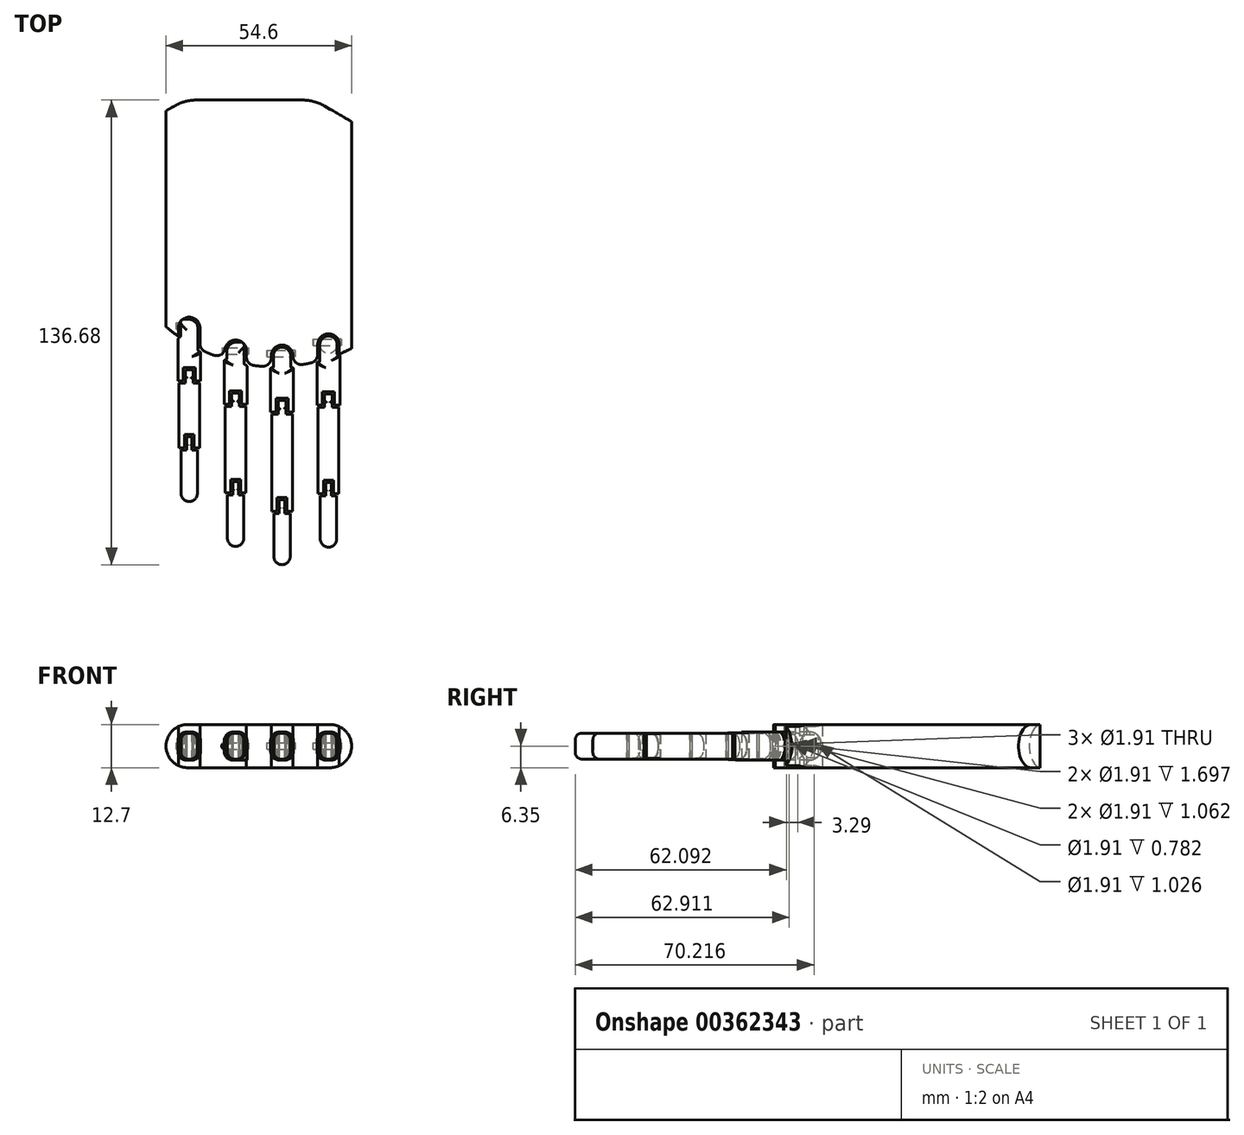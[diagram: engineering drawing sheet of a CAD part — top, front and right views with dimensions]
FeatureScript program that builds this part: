
annotation { "Feature Type Name" : "Feature", "Feature Type Description" : "" }
export const myFeature = defineFeature(function(context is Context, id is Id, definition is map)
    precondition{}
    {
        {
            var Q0;
            Q0=qCreatedBy(makeId("Top.planeOp"),FACE);
            var sketch = newSketch(context, id + "F0", { "sketchPlane" : qUnion([Q0])});
            skLineSegment(sketch, "E0", {"start": v(-15.65, 0) * mm, "end": v(15.65, 0) * mm});
            skLineSegment(sketch, "E1", {"start": v(-22, -1.7) * mm, "end": v(-24.55, -3.17) * mm});
            skLineSegment(sketch, "E2", {"start": v(22, -1.7) * mm, "end": v(30.05, -6.35) * mm});
            skPoint(sketch, "E3.visualSharp", {"position": v(-19.05, 0) * mm});
            skArc(sketch, "E3.filletArc", {"start": v(-15.65, 0) * mm, "mid": v(-18.93, -0.43) * mm, "end": v(-22, -1.7) * mm});
            skPoint(sketch, "E4.visualSharp", {"position": v(19.05, 0) * mm});
            skArc(sketch, "E4.filletArc", {"start": v(22, -1.7) * mm, "mid": v(18.93, -0.43) * mm, "end": v(15.65, 0) * mm});
            skLineSegment(sketch, "E5", {"start": v(-24.55, -3.17) * mm, "end": v(-24.55, -66.68) * mm});
            skLineSegment(sketch, "E6", {"start": v(30.05, -6.35) * mm, "end": v(30.05, -73.03) * mm});
            skArc(sketch, "E7", {"start": v(-24.55, -66.68) * mm, "mid": v(1.79, -78.13) * mm, "end": v(30.05, -73.03) * mm});
            skSolve(sketch);
        }
        {
            var Q0;
            Q0 = qSketchRegion(id + "F0", true);
            extrude(context, id + "F1", {"entities" : qUnion([Q0]), "depth" : 12.7 * mm});
        }
        {
            var Q0;
            Q0=makeQuery(id+"F1.opExtrude","CAP_FACE",FACE,{"disambiguationData":[OSD([sQuery(id+"F0.wireOp",EDGE,"E0"),sQuery(id+"F0.wireOp",EDGE,"E1"),sQuery(id+"F0.wireOp",EDGE,"E2"),sQuery(id+"F0.wireOp",EDGE,"E3.filletArc"),sQuery(id+"F0.wireOp",EDGE,"E4.filletArc"),sQuery(id+"F0.wireOp",EDGE,"E5"),sQuery(id+"F0.wireOp",EDGE,"E6"),sQuery(id+"F0.wireOp",EDGE,"E7")])],"isStart":false});
            var sketch = newSketch(context, id + "F2", { "sketchPlane" : qUnion([Q0])});
            skLineSegment(sketch, "E8.bottom", {"start": v(20.05, -68.76) * mm, "end": v(26.4, -68.76) * mm});
            skLineSegment(sketch, "E8.top", {"start": v(20.05, -81.46) * mm, "end": v(26.4, -81.46) * mm});
            skLineSegment(sketch, "E8.left", {"start": v(20.05, -68.76) * mm, "end": v(20.05, -81.46) * mm});
            skLineSegment(sketch, "E8.right", {"start": v(26.4, -68.76) * mm, "end": v(26.4, -81.46) * mm});
            skLineSegment(sketch, "E9.bottom", {"start": v(6.4, -72.05) * mm, "end": v(12.75, -72.05) * mm});
            skLineSegment(sketch, "E9.top", {"start": v(6.4, -84.75) * mm, "end": v(12.75, -84.75) * mm});
            skLineSegment(sketch, "E9.left", {"start": v(6.4, -72.05) * mm, "end": v(6.4, -84.75) * mm});
            skLineSegment(sketch, "E9.right", {"start": v(12.75, -72.05) * mm, "end": v(12.75, -84.75) * mm});
            skLineSegment(sketch, "E10.bottom", {"start": v(-7.25, -70.6) * mm, "end": v(-0.9, -70.6) * mm});
            skLineSegment(sketch, "E10.top", {"start": v(-7.25, -83.3) * mm, "end": v(-0.9, -83.3) * mm});
            skLineSegment(sketch, "E10.left", {"start": v(-7.25, -70.6) * mm, "end": v(-7.25, -83.3) * mm});
            skLineSegment(sketch, "E10.right", {"start": v(-0.9, -70.6) * mm, "end": v(-0.9, -83.3) * mm});
            skLineSegment(sketch, "E11.bottom", {"start": v(-20.9, -63.86) * mm, "end": v(-14.55, -63.86) * mm});
            skLineSegment(sketch, "E11.top", {"start": v(-20.9, -76.56) * mm, "end": v(-14.55, -76.56) * mm});
            skLineSegment(sketch, "E11.left", {"start": v(-20.9, -63.86) * mm, "end": v(-20.9, -76.56) * mm});
            skLineSegment(sketch, "E11.right", {"start": v(-14.55, -63.86) * mm, "end": v(-14.55, -76.56) * mm});
            skLineSegment(sketch, "E12", {"start": v(-24.55, -66.68) * mm, "end": v(30.05, -66.68) * mm, "construction": true});
            skLineSegment(sketch, "E13", {"start": v(-24.55, -70.2) * mm, "end": v(30.05, -70.2) * mm, "construction": true});
            skLineSegment(sketch, "E14", {"start": v(-10.78, -76.94) * mm, "end": v(0, -76.94) * mm, "construction": true});
            skLineSegment(sketch, "E15", {"start": v(14.95, -78.4) * mm, "end": v(7.26, -78.4) * mm, "construction": true});
            skLineSegment(sketch, "E16", {"start": v(22.41, -75.1) * mm, "end": v(20.87, -75.1) * mm, "construction": true});
            skLineSegment(sketch, "E17", {"start": v(-19.32, -68.57) * mm, "end": v(-19.32, -72.13) * mm, "construction": true});
            skLineSegment(sketch, "E18", {"start": v(-5.66, -75.3) * mm, "end": v(-5.66, -80.1) * mm, "construction": true});
            skLineSegment(sketch, "E19", {"start": v(7.99, -77.42) * mm, "end": v(7.99, -81.03) * mm, "construction": true});
            skLineSegment(sketch, "E20", {"start": v(21.64, -72.63) * mm, "end": v(21.64, -77.42) * mm, "construction": true});
            skPoint(sketch, "E20.startSnap0", {"position": v(21.64, -75.1) * mm});
            skSolve(sketch);
        }
        {
            var Q0;
            Q0 = qSketchRegion(id + "F2", true);
            extrude(context, id + "F3", {"entities" : qUnion([Q0]), "operationType" : NewBodyOperationType.REMOVE, "endBound" : BoundingType.UP_TO_NEXT, "oppositeDirection" : true, "depth" : 25.4 * mm});
        }
        {
            var Q0;
            Q0=qCreatedBy(makeId("Top.planeOp"),FACE);
            cPlane(context, id + "F4", {"entities" : qUnion([Q0]), "cplaneType" : CPlaneType.OFFSET, "offset" : 6.35 * mm, "width" : 152.4 * mm, "height" : 152.4 * mm});
        }
        {
            var Q0;
            Q0=qCreatedBy(id+"F4.planeOp",FACE);
            var sketch = newSketch(context, id + "F5", { "sketchPlane" : qUnion([Q0])});
            skLineSegment(sketch, "E21.bottom", {"start": v(-20.27, -64.5) * mm, "end": v(-15.19, -64.5) * mm});
            skLineSegment(sketch, "E21.left", {"start": v(-20.27, -64.5) * mm, "end": v(-20.27, -69.33) * mm});
            skLineSegment(sketch, "E21.right", {"start": v(-15.19, -64.5) * mm, "end": v(-15.19, -73.3) * mm});
            skLineSegment(sketch, "E22", {"start": v(-21.07, -70.6) * mm, "end": v(-21.07, -82.67) * mm});
            skLineSegment(sketch, "E23", {"start": v(-14.36, -82.67) * mm, "end": v(-14.36, -74.5) * mm});
            skArc(sketch, "E24", {"start": v(-14.84, -73.88) * mm, "mid": v(-14.78, -73.9) * mm, "end": v(-14.71, -73.94) * mm});
            skPoint(sketch, "E25.visualSharp", {"position": v(-15.19, -73.7) * mm});
            skArc(sketch, "E25.filletArc", {"start": v(-15.19, -73.3) * mm, "mid": v(-15.1, -73.64) * mm, "end": v(-14.84, -73.88) * mm});
            skPoint(sketch, "E26.visualSharp", {"position": v(-14.36, -74.11) * mm});
            skArc(sketch, "E26.filletArc", {"start": v(-14.36, -74.5) * mm, "mid": v(-14.46, -74.17) * mm, "end": v(-14.71, -73.94) * mm});
            skLineSegment(sketch, "E27", {"start": v(-21.07, -82.67) * mm, "end": v(-19.48, -82.67) * mm});
            skLineSegment(sketch, "E28", {"start": v(-19.48, -82.67) * mm, "end": v(-19.48, -78.69) * mm});
            skLineSegment(sketch, "E29", {"start": v(-19.48, -78.69) * mm, "end": v(-15.95, -78.69) * mm});
            skLineSegment(sketch, "E30", {"start": v(-15.95, -78.69) * mm, "end": v(-15.95, -82.67) * mm});
            skLineSegment(sketch, "E31", {"start": v(-15.95, -82.67) * mm, "end": v(-14.36, -82.67) * mm});
            skLineSegment(sketch, "E32.bottom", {"start": v(-6.62, -71.23) * mm, "end": v(-1.54, -71.23) * mm});
            skLineSegment(sketch, "E32.left", {"start": v(-6.62, -71.23) * mm, "end": v(-6.62, -75.87) * mm});
            skLineSegment(sketch, "E33", {"start": v(-1.54, -71.23) * mm, "end": v(-1.54, -77.58) * mm});
            skLineSegment(sketch, "E34", {"start": v(7.04, -78.4) * mm, "end": v(7.04, -72.68) * mm});
            skLineSegment(sketch, "E35", {"start": v(7.04, -72.68) * mm, "end": v(12.12, -72.68) * mm});
            skLineSegment(sketch, "E36", {"start": v(12.12, -72.68) * mm, "end": v(12.12, -78.4) * mm});
            skLineSegment(sketch, "E37", {"start": v(20.69, -76.73) * mm, "end": v(20.69, -69.4) * mm});
            skLineSegment(sketch, "E38", {"start": v(20.69, -69.4) * mm, "end": v(25.77, -69.4) * mm});
            skLineSegment(sketch, "E39", {"start": v(25.77, -69.4) * mm, "end": v(25.77, -74.6) * mm});
            skPoint(sketch, "E40.visualSharp", {"position": v(-21.07, -69.97) * mm});
            skPoint(sketch, "E41.visualSharp", {"position": v(-20.27, -69.97) * mm});
            skLineSegment(sketch, "E42", {"start": v(-7.43, -76.84) * mm, "end": v(-7.43, -89.54) * mm});
            skLineSegment(sketch, "E43", {"start": v(-7.43, -89.54) * mm, "end": v(-5.84, -89.54) * mm});
            skLineSegment(sketch, "E44", {"start": v(-5.84, -89.54) * mm, "end": v(-5.84, -85.55) * mm});
            skLineSegment(sketch, "E45", {"start": v(-5.84, -85.55) * mm, "end": v(-2.31, -85.55) * mm});
            skLineSegment(sketch, "E46", {"start": v(-2.31, -85.55) * mm, "end": v(-2.31, -89.54) * mm});
            skLineSegment(sketch, "E47", {"start": v(-2.31, -89.54) * mm, "end": v(-0.72, -89.54) * mm});
            skLineSegment(sketch, "E48", {"start": v(-0.72, -89.54) * mm, "end": v(-0.72, -78.5) * mm});
            skPoint(sketch, "E49.visualSharp", {"position": v(-6.62, -76.4) * mm});
            skPoint(sketch, "E50.visualSharp", {"position": v(-7.43, -76.4) * mm});
            skPoint(sketch, "E51.visualSharp", {"position": v(-1.54, -78.22) * mm});
            skArc(sketch, "E51.filletArc", {"start": v(-1.54, -77.58) * mm, "mid": v(-1.37, -77.79) * mm, "end": v(-1.13, -77.91) * mm});
            skPoint(sketch, "E52.visualSharp", {"position": v(-0.72, -78.22) * mm});
            skArc(sketch, "E52.filletArc", {"start": v(-0.72, -78.5) * mm, "mid": v(-0.84, -78.15) * mm, "end": v(-1.13, -77.91) * mm});
            skLineSegment(sketch, "E53.bottom", {"start": v(6.54, -78.72) * mm, "end": v(6.72, -78.72) * mm});
            skLineSegment(sketch, "E53.left", {"start": v(6.22, -79.03) * mm, "end": v(6.22, -91.73) * mm});
            skLineSegment(sketch, "E53.right", {"start": v(12.93, -79.03) * mm, "end": v(12.93, -91.73) * mm});
            skLineSegment(sketch, "E54.trimOffspring", {"start": v(12.43, -78.72) * mm, "end": v(12.61, -78.72) * mm});
            skPoint(sketch, "E55.visualSharp", {"position": v(7.04, -78.72) * mm});
            skArc(sketch, "E55.filletArc", {"start": v(6.72, -78.72) * mm, "mid": v(6.94, -78.62) * mm, "end": v(7.04, -78.4) * mm});
            skPoint(sketch, "E56.visualSharp", {"position": v(12.12, -78.72) * mm});
            skArc(sketch, "E56.filletArc", {"start": v(12.12, -78.4) * mm, "mid": v(12.2, -78.62) * mm, "end": v(12.43, -78.72) * mm});
            skLineSegment(sketch, "E57", {"start": v(6.22, -91.73) * mm, "end": v(7.81, -91.73) * mm});
            skLineSegment(sketch, "E58", {"start": v(7.81, -91.73) * mm, "end": v(7.81, -87.75) * mm});
            skLineSegment(sketch, "E59", {"start": v(7.81, -87.75) * mm, "end": v(11.34, -87.75) * mm});
            skLineSegment(sketch, "E60", {"start": v(11.34, -87.75) * mm, "end": v(11.34, -91.73) * mm});
            skLineSegment(sketch, "E61", {"start": v(11.34, -91.73) * mm, "end": v(12.93, -91.73) * mm});
            skPoint(sketch, "E62.visualSharp", {"position": v(6.22, -78.72) * mm});
            skArc(sketch, "E62.filletArc", {"start": v(6.54, -78.72) * mm, "mid": v(6.32, -78.8) * mm, "end": v(6.22, -79.03) * mm});
            skPoint(sketch, "E63.visualSharp", {"position": v(12.93, -78.72) * mm});
            skArc(sketch, "E63.filletArc", {"start": v(12.93, -79.03) * mm, "mid": v(12.84, -78.8) * mm, "end": v(12.61, -78.72) * mm});
            skArc(sketch, "E64", {"start": v(-7.03, -76.36) * mm, "mid": v(-6.73, -76.19) * mm, "end": v(-6.62, -75.87) * mm});
            skArc(sketch, "E65", {"start": v(-7.03, -76.36) * mm, "mid": v(-7.32, -76.53) * mm, "end": v(-7.43, -76.84) * mm});
            skArc(sketch, "E66", {"start": v(-20.67, -69.88) * mm, "mid": v(-20.96, -70.2) * mm, "end": v(-21.07, -70.6) * mm});
            skArc(sketch, "E67", {"start": v(-20.67, -69.88) * mm, "mid": v(-20.38, -69.67) * mm, "end": v(-20.27, -69.33) * mm});
            skLineSegment(sketch, "E68", {"start": v(20.37, -77.04) * mm, "end": v(20.2, -77.04) * mm});
            skLineSegment(sketch, "E69", {"start": v(19.88, -77.36) * mm, "end": v(19.88, -89.74) * mm});
            skLineSegment(sketch, "E70", {"start": v(19.88, -89.74) * mm, "end": v(21.46, -89.74) * mm});
            skLineSegment(sketch, "E71", {"start": v(21.46, -89.74) * mm, "end": v(21.46, -85.76) * mm});
            skLineSegment(sketch, "E72", {"start": v(21.46, -85.76) * mm, "end": v(25, -85.76) * mm});
            skLineSegment(sketch, "E73", {"start": v(25, -85.76) * mm, "end": v(25, -89.74) * mm});
            skLineSegment(sketch, "E74", {"start": v(25, -89.74) * mm, "end": v(26.58, -89.74) * mm});
            skLineSegment(sketch, "E75", {"start": v(26.58, -89.74) * mm, "end": v(26.58, -75.24) * mm});
            skLineSegment(sketch, "E76", {"start": v(26.26, -74.92) * mm, "end": v(26.09, -74.92) * mm});
            skPoint(sketch, "E77.visualSharp", {"position": v(19.88, -77.04) * mm});
            skArc(sketch, "E77.filletArc", {"start": v(20.2, -77.04) * mm, "mid": v(19.97, -77.14) * mm, "end": v(19.88, -77.36) * mm});
            skPoint(sketch, "E78.visualSharp", {"position": v(20.69, -77.04) * mm});
            skArc(sketch, "E78.filletArc", {"start": v(20.37, -77.04) * mm, "mid": v(20.6, -76.95) * mm, "end": v(20.69, -76.73) * mm});
            skPoint(sketch, "E79.visualSharp", {"position": v(25.77, -74.92) * mm});
            skArc(sketch, "E79.filletArc", {"start": v(25.77, -74.6) * mm, "mid": v(25.86, -74.83) * mm, "end": v(26.09, -74.92) * mm});
            skPoint(sketch, "E80.visualSharp", {"position": v(26.58, -74.92) * mm});
            skArc(sketch, "E80.filletArc", {"start": v(26.58, -75.24) * mm, "mid": v(26.49, -75.02) * mm, "end": v(26.26, -74.92) * mm});
            skSolve(sketch);
        }
        {
            var Q0;
            Q0 = qSketchRegion(id + "F5", true);
            extrude(context, id + "F6", {"entities" : qUnion([Q0]), "endBound" : BoundingType.SYMMETRIC, "depth" : 8.25 * mm});
        }
        {
            var Q0;
            Q0=makeQuery(id+"F6.opExtrude","CAP_EDGE",EDGE,{"disambiguationData":[OSD([sQuery(id+"F5.wireOp",EDGE,"E38")])],"isStart":false});
            var Q1;
            Q1=makeQuery(id+"F6.opExtrude","CAP_EDGE",EDGE,{"disambiguationData":[OSD([sQuery(id+"F5.wireOp",EDGE,"E38")])],"isStart":true});
            var Q2;
            Q2=makeQuery(id+"F6.opExtrude","CAP_EDGE",EDGE,{"disambiguationData":[OSD([sQuery(id+"F5.wireOp",EDGE,"E35")])],"isStart":false});
            var Q3;
            Q3=makeQuery(id+"F6.opExtrude","CAP_EDGE",EDGE,{"disambiguationData":[OSD([sQuery(id+"F5.wireOp",EDGE,"E35")])],"isStart":true});
            var Q4;
            Q4=makeQuery(id+"F6.opExtrude","CAP_EDGE",EDGE,{"disambiguationData":[OSD([sQuery(id+"F5.wireOp",EDGE,"E32.bottom")])],"isStart":true});
            var Q5;
            Q5=makeQuery(id+"F6.opExtrude","CAP_EDGE",EDGE,{"disambiguationData":[OSD([sQuery(id+"F5.wireOp",EDGE,"E21.bottom")])],"isStart":true});
            var Q6;
            Q6=makeQuery(id+"F6.opExtrude","CAP_EDGE",EDGE,{"disambiguationData":[OSD([sQuery(id+"F5.wireOp",EDGE,"E21.bottom")])],"isStart":false});
            var Q7;
            Q7=makeQuery(id+"F6.opExtrude","CAP_EDGE",EDGE,{"disambiguationData":[OSD([sQuery(id+"F5.wireOp",EDGE,"E32.bottom")])],"isStart":false});
            fillet(context, id + "F7", {"entities" : qUnion([Q0, Q1, Q2, Q3, Q4, Q5, Q6, Q7]), "radius" : 3.17 * mm, "tangentPropagation" : true, "allowEdgeOverflow" : false});
        }
        {
            var Q0;
            Q0=makeQuery(id+"F1.opExtrude","CAP_EDGE",EDGE,{"disambiguationData":[OSD([sQuery(id+"F0.wireOp",EDGE,"E5")])],"isStart":false});
            var Q1;
            Q1=makeQuery(id+"F1.opExtrude","CAP_EDGE",EDGE,{"disambiguationData":[OSD([sQuery(id+"F0.wireOp",EDGE,"E5")])],"isStart":true});
            var Q2;
            Q2=makeQuery(id+"F1.opExtrude","CAP_EDGE",EDGE,{"disambiguationData":[OSD([sQuery(id+"F0.wireOp",EDGE,"E6")])],"isStart":false});
            var Q3;
            Q3=makeQuery(id+"F1.opExtrude","CAP_EDGE",EDGE,{"disambiguationData":[OSD([sQuery(id+"F0.wireOp",EDGE,"E6")])],"isStart":true});
            fillet(context, id + "F8", {"entities" : qUnion([Q0, Q1, Q2, Q3]), "radius" : 6.35 * mm, "tangentPropagation" : true, "allowEdgeOverflow" : false});
        }
        {
            var Q0;
            Q0=makeQuery(id+"F3.boolean.opBoolean","COPY",EDGE,{"derivedFrom":makeQuery(id+"F3.opExtrude","SWEPT_EDGE",EDGE,{"disambiguationData":[OSD([sQuery(id+"F2.wireOp",EDGE,"E11.bottom"),sQuery(id+"F2.wireOp",EDGE,"E11.left")])]})});
            var Q1;
            Q1=makeQuery(id+"F3.boolean.opBoolean","COPY",EDGE,{"derivedFrom":makeQuery(id+"F3.opExtrude","SWEPT_EDGE",EDGE,{"disambiguationData":[OSD([sQuery(id+"F2.wireOp",EDGE,"E11.bottom"),sQuery(id+"F2.wireOp",EDGE,"E11.right")])]})});
            var Q2;
            Q2=makeQuery(id+"F3.boolean.opBoolean","COPY",EDGE,{"derivedFrom":makeQuery(id+"F3.opExtrude","SWEPT_EDGE",EDGE,{"disambiguationData":[OSD([sQuery(id+"F2.wireOp",EDGE,"E10.bottom"),sQuery(id+"F2.wireOp",EDGE,"E10.left")])]})});
            var Q3;
            Q3=makeQuery(id+"F3.boolean.opBoolean","COPY",EDGE,{"derivedFrom":makeQuery(id+"F3.opExtrude","SWEPT_EDGE",EDGE,{"disambiguationData":[OSD([sQuery(id+"F2.wireOp",EDGE,"E10.bottom"),sQuery(id+"F2.wireOp",EDGE,"E10.right")])]})});
            var Q4;
            Q4=makeQuery(id+"F3.boolean.opBoolean","COPY",EDGE,{"derivedFrom":makeQuery(id+"F3.opExtrude","SWEPT_EDGE",EDGE,{"disambiguationData":[OSD([sQuery(id+"F2.wireOp",EDGE,"E9.bottom"),sQuery(id+"F2.wireOp",EDGE,"E9.right")])]})});
            var Q5;
            Q5=makeQuery(id+"F3.boolean.opBoolean","COPY",EDGE,{"derivedFrom":makeQuery(id+"F3.opExtrude","SWEPT_EDGE",EDGE,{"disambiguationData":[OSD([sQuery(id+"F2.wireOp",EDGE,"E8.bottom"),sQuery(id+"F2.wireOp",EDGE,"E8.right")])]})});
            var Q6;
            Q6=makeQuery(id+"F3.boolean.opBoolean","COPY",EDGE,{"derivedFrom":makeQuery(id+"F3.opExtrude","SWEPT_EDGE",EDGE,{"disambiguationData":[OSD([sQuery(id+"F2.wireOp",EDGE,"E9.bottom"),sQuery(id+"F2.wireOp",EDGE,"E9.left")])]})});
            var Q7;
            Q7=makeQuery(id+"F3.boolean.opBoolean","COPY",EDGE,{"derivedFrom":makeQuery(id+"F3.opExtrude","SWEPT_EDGE",EDGE,{"disambiguationData":[OSD([sQuery(id+"F2.wireOp",EDGE,"E8.bottom"),sQuery(id+"F2.wireOp",EDGE,"E8.left")])]})});
            fillet(context, id + "F9", {"entities" : qUnion([Q0, Q1, Q2, Q3, Q4, Q5, Q6, Q7]), "radius" : 3.17 * mm, "tangentPropagation" : true, "allowEdgeOverflow" : false});
        }
        {
            var Q0;
            {var subQ0=sQuery(id+"F0.wireOp",EDGE,"E7");var subQ1=sQuery(id+"F2.wireOp",EDGE,"E10.left");Q0=makeQuery(id+"F3.boolean.opBoolean","COPY",EDGE,{"derivedFrom":makeQuery(id+"F3.opExtrude","CAP_EDGE",EDGE,{"disambiguationData":[OSD([subQ1]),topologyDisambiguationEdgeConnected([makeQuery(id+"F1.opExtrude","SWEPT_FACE",FACE,{"disambiguationData":[OSD([subQ0])]})])],"isStart":false})});}
            var Q1;
            Q1=makeQuery(id+"F3.boolean.opBoolean","COPY",EDGE,{"derivedFrom":makeQuery(id+"F3.opExtrude","CAP_EDGE",EDGE,{"disambiguationData":[OSD([sQuery(id+"F2.wireOp",EDGE,"E11.right")]),topologyDisambiguationEdgeConnected([makeQuery(id+"F1.opExtrude","SWEPT_FACE",FACE,{"disambiguationData":[OSD([sQuery(id+"F0.wireOp",EDGE,"E7")])]})])],"isStart":false})});
            var Q2;
            {var subQ0=sQuery(id+"F0.wireOp",EDGE,"E7");var subQ1=sQuery(id+"F2.wireOp",EDGE,"E10.right");Q2=makeQuery(id+"F3.boolean.opBoolean","COPY",EDGE,{"derivedFrom":makeQuery(id+"F3.opExtrude","CAP_EDGE",EDGE,{"disambiguationData":[OSD([subQ1]),topologyDisambiguationEdgeConnected([makeQuery(id+"F1.opExtrude","SWEPT_FACE",FACE,{"disambiguationData":[OSD([subQ0])]})])],"isStart":false})});}
            var Q3;
            {var subQ0=sQuery(id+"F0.wireOp",EDGE,"E7");var subQ1=sQuery(id+"F2.wireOp",EDGE,"E9.left");Q3=makeQuery(id+"F3.boolean.opBoolean","COPY",EDGE,{"derivedFrom":makeQuery(id+"F3.opExtrude","CAP_EDGE",EDGE,{"disambiguationData":[OSD([subQ1]),topologyDisambiguationEdgeConnected([makeQuery(id+"F1.opExtrude","SWEPT_FACE",FACE,{"disambiguationData":[OSD([subQ0])]})])],"isStart":false})});}
            var Q4;
            {var subQ0=sQuery(id+"F0.wireOp",EDGE,"E7");var subQ1=sQuery(id+"F2.wireOp",EDGE,"E9.right");Q4=makeQuery(id+"F3.boolean.opBoolean","COPY",EDGE,{"derivedFrom":makeQuery(id+"F3.opExtrude","CAP_EDGE",EDGE,{"disambiguationData":[OSD([subQ1]),topologyDisambiguationEdgeConnected([makeQuery(id+"F1.opExtrude","SWEPT_FACE",FACE,{"disambiguationData":[OSD([subQ0])]})])],"isStart":false})});}
            var Q5;
            {var subQ0=sQuery(id+"F0.wireOp",EDGE,"E7");var subQ1=sQuery(id+"F2.wireOp",EDGE,"E8.left");Q5=makeQuery(id+"F3.boolean.opBoolean","COPY",EDGE,{"derivedFrom":makeQuery(id+"F3.opExtrude","CAP_EDGE",EDGE,{"disambiguationData":[OSD([subQ1]),topologyDisambiguationEdgeConnected([makeQuery(id+"F1.opExtrude","SWEPT_FACE",FACE,{"disambiguationData":[OSD([subQ0])]})])],"isStart":false})});}
            fillet(context, id + "F10", {"entities" : qUnion([Q0, Q1, Q2, Q3, Q4, Q5]), "radius" : 2.54 * mm, "tangentPropagation" : true, "allowEdgeOverflow" : false});
        }
        {
            var Q0;
            Q0=makeQuery(id+"F6.opExtrude","CAP_EDGE",EDGE,{"disambiguationData":[OSD([sQuery(id+"F5.wireOp",EDGE,"E42")])],"isStart":false});
            var Q1;
            Q1=makeQuery(id+"F6.opExtrude","CAP_EDGE",EDGE,{"disambiguationData":[OSD([sQuery(id+"F5.wireOp",EDGE,"E48")])],"isStart":false});
            var Q2;
            Q2=makeQuery(id+"F6.opExtrude","CAP_EDGE",EDGE,{"disambiguationData":[OSD([sQuery(id+"F5.wireOp",EDGE,"E23")])],"isStart":false});
            var Q3;
            Q3=makeQuery(id+"F6.opExtrude","CAP_EDGE",EDGE,{"disambiguationData":[OSD([sQuery(id+"F5.wireOp",EDGE,"E22")])],"isStart":false});
            var Q4;
            Q4=makeQuery(id+"F6.opExtrude","CAP_EDGE",EDGE,{"disambiguationData":[OSD([sQuery(id+"F5.wireOp",EDGE,"E53.left")])],"isStart":false});
            var Q5;
            Q5=makeQuery(id+"F6.opExtrude","CAP_EDGE",EDGE,{"disambiguationData":[OSD([sQuery(id+"F5.wireOp",EDGE,"E53.right")])],"isStart":false});
            var Q6;
            Q6=makeQuery(id+"F6.opExtrude","CAP_EDGE",EDGE,{"disambiguationData":[OSD([sQuery(id+"F5.wireOp",EDGE,"E69")])],"isStart":false});
            var Q7;
            Q7=makeQuery(id+"F6.opExtrude","CAP_EDGE",EDGE,{"disambiguationData":[OSD([sQuery(id+"F5.wireOp",EDGE,"E75")])],"isStart":false});
            fillet(context, id + "F11", {"entities" : qUnion([Q0, Q1, Q2, Q3, Q4, Q5, Q6, Q7]), "radius" : 2.54 * mm, "tangentPropagation" : true, "allowEdgeOverflow" : false});
        }
        {
            var Q0;
            Q0=makeQuery(id+"F6.opExtrude","CAP_EDGE",EDGE,{"disambiguationData":[OSD([sQuery(id+"F5.wireOp",EDGE,"E22")])],"isStart":true});
            fillet(context, id + "F12", {"entities" : qUnion([Q0]), "radius" : 2.54 * mm, "tangentPropagation" : true, "allowEdgeOverflow" : false});
        }
        {
            var Q0;
            Q0=qCreatedBy(id+"F4.planeOp",FACE);
            var sketch = newSketch(context, id + "F13", { "sketchPlane" : qUnion([Q0])});
            skLineSegment(sketch, "E81.bottom", {"start": v(-18.85, -79.32) * mm, "end": v(-16.59, -79.32) * mm});
            skLineSegment(sketch, "E81.left", {"start": v(-18.85, -79.32) * mm, "end": v(-18.85, -83.3) * mm});
            skLineSegment(sketch, "E81.right", {"start": v(-16.59, -79.32) * mm, "end": v(-16.59, -83.3) * mm});
            skLineSegment(sketch, "E82", {"start": v(-18.85, -83.3) * mm, "end": v(-20.75, -83.3) * mm});
            skLineSegment(sketch, "E83", {"start": v(-20.75, -83.3) * mm, "end": v(-20.75, -102.35) * mm});
            skLineSegment(sketch, "E84", {"start": v(-20.75, -102.35) * mm, "end": v(-19.16, -102.35) * mm});
            skLineSegment(sketch, "E85", {"start": v(-14.68, -102.35) * mm, "end": v(-14.68, -83.3) * mm});
            skLineSegment(sketch, "E86", {"start": v(-14.68, -83.3) * mm, "end": v(-16.59, -83.3) * mm});
            skLineSegment(sketch, "E87.top", {"start": v(-19.16, -98.36) * mm, "end": v(-16.27, -98.36) * mm});
            skLineSegment(sketch, "E87.left", {"start": v(-19.16, -102.35) * mm, "end": v(-19.16, -98.36) * mm});
            skLineSegment(sketch, "E87.right", {"start": v(-16.27, -102.35) * mm, "end": v(-16.27, -98.36) * mm});
            skLineSegment(sketch, "E88.trimOffspring", {"start": v(-16.27, -102.35) * mm, "end": v(-14.68, -102.35) * mm});
            skLineSegment(sketch, "E89.bottom", {"start": v(-5.2, -86.18) * mm, "end": v(-2.95, -86.18) * mm});
            skLineSegment(sketch, "E89.left", {"start": v(-5.2, -86.18) * mm, "end": v(-5.2, -90.17) * mm});
            skLineSegment(sketch, "E89.right", {"start": v(-2.95, -86.18) * mm, "end": v(-2.95, -90.17) * mm});
            skLineSegment(sketch, "E90.bottom", {"start": v(-7.11, -90.17) * mm, "end": v(-5.2, -90.17) * mm});
            skLineSegment(sketch, "E90.top", {"start": v(-7.11, -115.57) * mm, "end": v(-5.52, -115.57) * mm});
            skLineSegment(sketch, "E90.left", {"start": v(-7.11, -90.17) * mm, "end": v(-7.11, -115.57) * mm});
            skLineSegment(sketch, "E90.right", {"start": v(-1.04, -90.17) * mm, "end": v(-1.04, -115.57) * mm});
            skLineSegment(sketch, "E91.bottom", {"start": v(-5.52, -111.58) * mm, "end": v(-2.63, -111.58) * mm});
            skLineSegment(sketch, "E91.left", {"start": v(-5.52, -111.58) * mm, "end": v(-5.52, -115.57) * mm});
            skLineSegment(sketch, "E91.right", {"start": v(-2.63, -111.58) * mm, "end": v(-2.63, -115.57) * mm});
            skLineSegment(sketch, "E92.bottom", {"start": v(8.45, -88.38) * mm, "end": v(10.7, -88.38) * mm});
            skLineSegment(sketch, "E92.left", {"start": v(8.45, -88.38) * mm, "end": v(8.45, -92.37) * mm});
            skLineSegment(sketch, "E92.right", {"start": v(10.7, -88.38) * mm, "end": v(10.7, -92.37) * mm});
            skLineSegment(sketch, "E93.bottom", {"start": v(6.54, -92.37) * mm, "end": v(8.45, -92.37) * mm});
            skLineSegment(sketch, "E93.top", {"start": v(6.54, -120.94) * mm, "end": v(8.13, -120.94) * mm});
            skLineSegment(sketch, "E93.left", {"start": v(6.54, -92.37) * mm, "end": v(6.54, -120.94) * mm});
            skLineSegment(sketch, "E93.right", {"start": v(12.61, -92.37) * mm, "end": v(12.61, -120.94) * mm});
            skLineSegment(sketch, "E94.bottom", {"start": v(8.13, -116.96) * mm, "end": v(11.02, -116.96) * mm});
            skLineSegment(sketch, "E94.left", {"start": v(8.13, -116.96) * mm, "end": v(8.13, -120.94) * mm});
            skLineSegment(sketch, "E94.right", {"start": v(11.02, -116.96) * mm, "end": v(11.02, -120.94) * mm});
            skLineSegment(sketch, "E95.bottom", {"start": v(22.1, -86.4) * mm, "end": v(24.36, -86.4) * mm});
            skLineSegment(sketch, "E95.left", {"start": v(22.1, -86.4) * mm, "end": v(22.1, -90.38) * mm});
            skLineSegment(sketch, "E95.right", {"start": v(24.36, -86.4) * mm, "end": v(24.36, -90.38) * mm});
            skLineSegment(sketch, "E96.bottom", {"start": v(20.2, -90.38) * mm, "end": v(22.1, -90.38) * mm});
            skLineSegment(sketch, "E96.top", {"start": v(20.2, -115.78) * mm, "end": v(21.78, -115.78) * mm});
            skLineSegment(sketch, "E96.left", {"start": v(20.2, -90.38) * mm, "end": v(20.2, -115.78) * mm});
            skLineSegment(sketch, "E96.right", {"start": v(26.26, -90.38) * mm, "end": v(26.26, -115.78) * mm});
            skLineSegment(sketch, "E97.bottom", {"start": v(21.78, -111.8) * mm, "end": v(24.68, -111.8) * mm});
            skLineSegment(sketch, "E97.left", {"start": v(21.78, -111.8) * mm, "end": v(21.78, -115.78) * mm});
            skLineSegment(sketch, "E97.right", {"start": v(24.68, -111.8) * mm, "end": v(24.68, -115.78) * mm});
            skLineSegment(sketch, "E98.trimOffspring", {"start": v(-2.95, -90.17) * mm, "end": v(-1.04, -90.17) * mm});
            skLineSegment(sketch, "E99.trimOffspring", {"start": v(-2.63, -115.57) * mm, "end": v(-1.04, -115.57) * mm});
            skLineSegment(sketch, "E100.trimOffspring", {"start": v(10.7, -92.37) * mm, "end": v(12.61, -92.37) * mm});
            skLineSegment(sketch, "E101.trimOffspring", {"start": v(11.02, -120.94) * mm, "end": v(12.61, -120.94) * mm});
            skLineSegment(sketch, "E102.trimOffspring", {"start": v(24.36, -90.38) * mm, "end": v(26.26, -90.38) * mm});
            skLineSegment(sketch, "E103.trimOffspring", {"start": v(24.68, -115.78) * mm, "end": v(26.26, -115.78) * mm});
            skSolve(sketch);
        }
        {
            var Q0;
            Q0 = qSketchRegion(id + "F13", true);
            extrude(context, id + "F14", {"entities" : qUnion([Q0]), "endBound" : BoundingType.SYMMETRIC, "depth" : 7.62 * mm});
        }
        {
            var Q0;
            Q0=makeQuery(id+"F14.opExtrude","CAP_EDGE",EDGE,{"disambiguationData":[OSD([sQuery(id+"F13.wireOp",EDGE,"E83")])],"isStart":false});
            var Q1;
            Q1=makeQuery(id+"F14.opExtrude","CAP_EDGE",EDGE,{"disambiguationData":[OSD([sQuery(id+"F13.wireOp",EDGE,"E85")])],"isStart":false});
            var Q2;
            Q2=makeQuery(id+"F14.opExtrude","CAP_EDGE",EDGE,{"disambiguationData":[OSD([sQuery(id+"F13.wireOp",EDGE,"E83")])],"isStart":true});
            var Q3;
            Q3=makeQuery(id+"F14.opExtrude","CAP_EDGE",EDGE,{"disambiguationData":[OSD([sQuery(id+"F13.wireOp",EDGE,"E85")])],"isStart":true});
            var Q4;
            Q4=makeQuery(id+"F14.opExtrude","CAP_EDGE",EDGE,{"disambiguationData":[OSD([sQuery(id+"F13.wireOp",EDGE,"E90.left")])],"isStart":true});
            var Q5;
            Q5=makeQuery(id+"F14.opExtrude","CAP_EDGE",EDGE,{"disambiguationData":[OSD([sQuery(id+"F13.wireOp",EDGE,"E90.right")])],"isStart":true});
            var Q6;
            Q6=makeQuery(id+"F14.opExtrude","CAP_EDGE",EDGE,{"disambiguationData":[OSD([sQuery(id+"F13.wireOp",EDGE,"E93.left")])],"isStart":true});
            var Q7;
            Q7=makeQuery(id+"F14.opExtrude","CAP_EDGE",EDGE,{"disambiguationData":[OSD([sQuery(id+"F13.wireOp",EDGE,"E93.right")])],"isStart":true});
            var Q8;
            Q8=makeQuery(id+"F14.opExtrude","CAP_EDGE",EDGE,{"disambiguationData":[OSD([sQuery(id+"F13.wireOp",EDGE,"E96.left")])],"isStart":true});
            var Q9;
            Q9=makeQuery(id+"F14.opExtrude","CAP_EDGE",EDGE,{"disambiguationData":[OSD([sQuery(id+"F13.wireOp",EDGE,"E96.right")])],"isStart":true});
            var Q10;
            Q10=makeQuery(id+"F14.opExtrude","CAP_EDGE",EDGE,{"disambiguationData":[OSD([sQuery(id+"F13.wireOp",EDGE,"E96.left")])],"isStart":false});
            var Q11;
            Q11=makeQuery(id+"F14.opExtrude","CAP_EDGE",EDGE,{"disambiguationData":[OSD([sQuery(id+"F13.wireOp",EDGE,"E96.right")])],"isStart":false});
            var Q12;
            Q12=makeQuery(id+"F14.opExtrude","CAP_EDGE",EDGE,{"disambiguationData":[OSD([sQuery(id+"F13.wireOp",EDGE,"E93.right")])],"isStart":false});
            var Q13;
            Q13=makeQuery(id+"F14.opExtrude","CAP_EDGE",EDGE,{"disambiguationData":[OSD([sQuery(id+"F13.wireOp",EDGE,"E93.left")])],"isStart":false});
            var Q14;
            Q14=makeQuery(id+"F14.opExtrude","CAP_EDGE",EDGE,{"disambiguationData":[OSD([sQuery(id+"F13.wireOp",EDGE,"E90.right")])],"isStart":false});
            var Q15;
            Q15=makeQuery(id+"F14.opExtrude","CAP_EDGE",EDGE,{"disambiguationData":[OSD([sQuery(id+"F13.wireOp",EDGE,"E90.left")])],"isStart":false});
            fillet(context, id + "F15", {"entities" : qUnion([Q0, Q1, Q2, Q3, Q4, Q5, Q6, Q7, Q8, Q9, Q10, Q11, Q12, Q13, Q14, Q15]), "radius" : 2.54 * mm, "tangentPropagation" : true, "allowEdgeOverflow" : false});
        }
        {
            var Q0;
            Q0=makeQuery(id+"F14.opExtrude","CAP_EDGE",EDGE,{"disambiguationData":[OSD([sQuery(id+"F13.wireOp",EDGE,"E81.bottom")])],"isStart":false});
            var Q1;
            Q1=makeQuery(id+"F14.opExtrude","CAP_EDGE",EDGE,{"disambiguationData":[OSD([sQuery(id+"F13.wireOp",EDGE,"E89.bottom")])],"isStart":false});
            var Q2;
            Q2=makeQuery(id+"F14.opExtrude","CAP_EDGE",EDGE,{"disambiguationData":[OSD([sQuery(id+"F13.wireOp",EDGE,"E92.bottom")])],"isStart":false});
            var Q3;
            Q3=makeQuery(id+"F14.opExtrude","CAP_EDGE",EDGE,{"disambiguationData":[OSD([sQuery(id+"F13.wireOp",EDGE,"E95.bottom")])],"isStart":false});
            var Q4;
            Q4=makeQuery(id+"F14.opExtrude","CAP_EDGE",EDGE,{"disambiguationData":[OSD([sQuery(id+"F13.wireOp",EDGE,"E95.bottom")])],"isStart":true});
            var Q5;
            Q5=makeQuery(id+"F14.opExtrude","CAP_EDGE",EDGE,{"disambiguationData":[OSD([sQuery(id+"F13.wireOp",EDGE,"E92.bottom")])],"isStart":true});
            var Q6;
            Q6=makeQuery(id+"F14.opExtrude","CAP_EDGE",EDGE,{"disambiguationData":[OSD([sQuery(id+"F13.wireOp",EDGE,"E89.bottom")])],"isStart":true});
            var Q7;
            Q7=makeQuery(id+"F14.opExtrude","CAP_EDGE",EDGE,{"disambiguationData":[OSD([sQuery(id+"F13.wireOp",EDGE,"E81.bottom")])],"isStart":true});
            fillet(context, id + "F16", {"entities" : qUnion([Q0, Q1, Q2, Q3, Q4, Q5, Q6, Q7]), "radius" : 2.54 * mm, "tangentPropagation" : true, "allowEdgeOverflow" : false});
        }
        {
            var Q0;
            Q0=qCreatedBy(id+"F4.planeOp",FACE);
            var sketch = newSketch(context, id + "F17", { "sketchPlane" : qUnion([Q0])});
            skLineSegment(sketch, "E104.bottom", {"start": v(-18.53, -99) * mm, "end": v(-16.9, -99) * mm});
            skLineSegment(sketch, "E104.left", {"start": v(-18.53, -99) * mm, "end": v(-18.53, -102.99) * mm});
            skLineSegment(sketch, "E104.right", {"start": v(-16.9, -99) * mm, "end": v(-16.9, -102.99) * mm});
            skLineSegment(sketch, "E105.bottom", {"start": v(-20.12, -102.99) * mm, "end": v(-18.53, -102.99) * mm});
            skLineSegment(sketch, "E105.left", {"start": v(-20.12, -102.99) * mm, "end": v(-20.12, -115.69) * mm});
            skLineSegment(sketch, "E105.right", {"start": v(-15.32, -102.99) * mm, "end": v(-15.32, -115.69) * mm});
            skLineSegment(sketch, "E106.trimOffspring", {"start": v(-16.9, -102.99) * mm, "end": v(-15.32, -102.99) * mm});
            skArc(sketch, "E107", {"start": v(-20.12, -115.69) * mm, "mid": v(-17.72, -118.09) * mm, "end": v(-15.32, -115.69) * mm});
            skLineSegment(sketch, "E108.bottom", {"start": v(-4.89, -112.22) * mm, "end": v(-3.26, -112.22) * mm});
            skLineSegment(sketch, "E108.left", {"start": v(-4.89, -112.22) * mm, "end": v(-4.89, -116.2) * mm});
            skLineSegment(sketch, "E108.right", {"start": v(-3.26, -112.22) * mm, "end": v(-3.26, -116.2) * mm});
            skLineSegment(sketch, "E109.bottom", {"start": v(-6.48, -116.2) * mm, "end": v(-4.89, -116.2) * mm});
            skLineSegment(sketch, "E109.left", {"start": v(-6.48, -116.2) * mm, "end": v(-6.48, -128.9) * mm});
            skLineSegment(sketch, "E109.right", {"start": v(-1.68, -116.2) * mm, "end": v(-1.68, -128.9) * mm});
            skLineSegment(sketch, "E110.trimOffspring", {"start": v(-3.26, -116.2) * mm, "end": v(-1.68, -116.2) * mm});
            skArc(sketch, "E111", {"start": v(-6.48, -128.9) * mm, "mid": v(-4.08, -131.3) * mm, "end": v(-1.68, -128.9) * mm});
            skLineSegment(sketch, "E112.bottom", {"start": v(8.76, -117.6) * mm, "end": v(10.39, -117.6) * mm});
            skLineSegment(sketch, "E112.left", {"start": v(8.76, -117.6) * mm, "end": v(8.76, -121.58) * mm});
            skLineSegment(sketch, "E112.right", {"start": v(10.39, -117.6) * mm, "end": v(10.39, -121.58) * mm});
            skLineSegment(sketch, "E113.bottom", {"start": v(7.18, -121.58) * mm, "end": v(8.76, -121.58) * mm});
            skLineSegment(sketch, "E113.left", {"start": v(7.18, -121.58) * mm, "end": v(7.18, -134.28) * mm});
            skLineSegment(sketch, "E113.right", {"start": v(11.98, -121.58) * mm, "end": v(11.98, -134.28) * mm});
            skLineSegment(sketch, "E114.bottom", {"start": v(22.42, -112.43) * mm, "end": v(24.04, -112.43) * mm});
            skLineSegment(sketch, "E114.left", {"start": v(22.42, -112.43) * mm, "end": v(22.42, -116.41) * mm});
            skLineSegment(sketch, "E114.right", {"start": v(24.04, -112.43) * mm, "end": v(24.04, -116.41) * mm});
            skLineSegment(sketch, "E115.bottom", {"start": v(20.83, -116.41) * mm, "end": v(22.42, -116.41) * mm});
            skLineSegment(sketch, "E115.left", {"start": v(20.83, -116.41) * mm, "end": v(20.83, -129.11) * mm});
            skLineSegment(sketch, "E115.right", {"start": v(25.63, -116.41) * mm, "end": v(25.63, -129.11) * mm});
            skLineSegment(sketch, "E116.trimOffspring", {"start": v(24.04, -116.41) * mm, "end": v(25.63, -116.41) * mm});
            skLineSegment(sketch, "E117.trimOffspring", {"start": v(10.39, -121.58) * mm, "end": v(11.98, -121.58) * mm});
            skArc(sketch, "E118", {"start": v(7.18, -134.28) * mm, "mid": v(9.58, -136.68) * mm, "end": v(11.98, -134.28) * mm});
            skArc(sketch, "E119", {"start": v(20.83, -129.11) * mm, "mid": v(23.23, -131.51) * mm, "end": v(25.63, -129.11) * mm});
            skSolve(sketch);
        }
        {
            var Q0;
            Q0 = qSketchRegion(id + "F17", true);
            extrude(context, id + "F18", {"entities" : qUnion([Q0]), "endBound" : BoundingType.SYMMETRIC, "depth" : 7.62 * mm});
        }
        {
            var Q0;
            Q0=makeQuery(id+"F18.opExtrude","CAP_EDGE",EDGE,{"disambiguationData":[OSD([sQuery(id+"F17.wireOp",EDGE,"E105.right")])],"isStart":false});
            var Q1;
            Q1=makeQuery(id+"F18.opExtrude","CAP_EDGE",EDGE,{"disambiguationData":[OSD([sQuery(id+"F17.wireOp",EDGE,"E105.left")])],"isStart":false});
            var Q2;
            Q2=makeQuery(id+"F18.opExtrude","CAP_EDGE",EDGE,{"disambiguationData":[OSD([sQuery(id+"F17.wireOp",EDGE,"E109.left")])],"isStart":false});
            var Q3;
            Q3=makeQuery(id+"F18.opExtrude","CAP_EDGE",EDGE,{"disambiguationData":[OSD([sQuery(id+"F17.wireOp",EDGE,"E113.left")])],"isStart":false});
            var Q4;
            Q4=makeQuery(id+"F18.opExtrude","CAP_EDGE",EDGE,{"disambiguationData":[OSD([sQuery(id+"F17.wireOp",EDGE,"E115.left")])],"isStart":false});
            var Q5;
            Q5=makeQuery(id+"F18.opExtrude","CAP_EDGE",EDGE,{"disambiguationData":[OSD([sQuery(id+"F17.wireOp",EDGE,"E115.right")])],"isStart":true});
            var Q6;
            Q6=makeQuery(id+"F18.opExtrude","CAP_EDGE",EDGE,{"disambiguationData":[OSD([sQuery(id+"F17.wireOp",EDGE,"E113.right")])],"isStart":true});
            var Q7;
            Q7=makeQuery(id+"F18.opExtrude","CAP_EDGE",EDGE,{"disambiguationData":[OSD([sQuery(id+"F17.wireOp",EDGE,"E109.right")])],"isStart":true});
            var Q8;
            Q8=makeQuery(id+"F18.opExtrude","CAP_EDGE",EDGE,{"disambiguationData":[OSD([sQuery(id+"F17.wireOp",EDGE,"E105.right")])],"isStart":true});
            fillet(context, id + "F19", {"entities" : qUnion([Q0, Q1, Q2, Q3, Q4, Q5, Q6, Q7, Q8]), "radius" : 1.9 * mm, "tangentPropagation" : true, "allowEdgeOverflow" : false});
        }
        {
            var Q0;
            Q0=makeQuery(id+"F18.opExtrude","CAP_EDGE",EDGE,{"disambiguationData":[OSD([sQuery(id+"F17.wireOp",EDGE,"E104.bottom")])],"isStart":false});
            var Q1;
            Q1=makeQuery(id+"F18.opExtrude","CAP_EDGE",EDGE,{"disambiguationData":[OSD([sQuery(id+"F17.wireOp",EDGE,"E108.bottom")])],"isStart":false});
            var Q2;
            Q2=makeQuery(id+"F18.opExtrude","CAP_EDGE",EDGE,{"disambiguationData":[OSD([sQuery(id+"F17.wireOp",EDGE,"E112.bottom")])],"isStart":false});
            var Q3;
            Q3=makeQuery(id+"F18.opExtrude","CAP_EDGE",EDGE,{"disambiguationData":[OSD([sQuery(id+"F17.wireOp",EDGE,"E114.bottom")])],"isStart":false});
            var Q4;
            Q4=makeQuery(id+"F18.opExtrude","CAP_EDGE",EDGE,{"disambiguationData":[OSD([sQuery(id+"F17.wireOp",EDGE,"E104.bottom")])],"isStart":true});
            var Q5;
            Q5=makeQuery(id+"F18.opExtrude","CAP_EDGE",EDGE,{"disambiguationData":[OSD([sQuery(id+"F17.wireOp",EDGE,"E108.bottom")])],"isStart":true});
            var Q6;
            Q6=makeQuery(id+"F18.opExtrude","CAP_EDGE",EDGE,{"disambiguationData":[OSD([sQuery(id+"F17.wireOp",EDGE,"E112.bottom")])],"isStart":true});
            var Q7;
            Q7=makeQuery(id+"F18.opExtrude","CAP_EDGE",EDGE,{"disambiguationData":[OSD([sQuery(id+"F17.wireOp",EDGE,"E114.bottom")])],"isStart":true});
            fillet(context, id + "F20", {"entities" : qUnion([Q0, Q1, Q2, Q3, Q4, Q5, Q6, Q7]), "radius" : 2.54 * mm, "tangentPropagation" : true, "allowEdgeOverflow" : false});
        }
        {
            var Q0;
            Q0=makeQuery(id+"F6.opExtrude","SWEPT_FACE",FACE,{"disambiguationData":[OSD([sQuery(id+"F5.wireOp",EDGE,"E21.left")])]});
            var sketch = newSketch(context, id + "F21", { "sketchPlane" : qUnion([Q0])});
            skCircle(sketch, "E120", {"center": v(66.46, 6.35) * mm, "radius": 0.95 * mm});
            skSolve(sketch);
        }
        {
            var Q0;
            Q0 = qSketchRegion(id + "F21", true);
            var Q1;
            Q1=sQuery(id+"F21.wireOp",EDGE,"E120");
            extrude(context, id + "F22", {"entities" : qUnion([Q0]), "operationType" : NewBodyOperationType.ADD, "surfaceEntities" : qUnion([Q1]), "depth" : 1.27 * mm});
        }
        {
            var Q0;
            Q0=makeQuery(id+"F3.boolean.opBoolean","COPY",FACE,{"derivedFrom":makeQuery(id+"F3.opExtrude","SWEPT_FACE",FACE,{"disambiguationData":[OSD([sQuery(id+"F2.wireOp",EDGE,"E11.left")])]})});
            var sketch = newSketch(context, id + "F23", { "sketchPlane" : qUnion([Q0])});
            skCircle(sketch, "E121", {"center": v(-66.46, 6.35) * mm, "radius": 0.95 * mm});
            skSolve(sketch);
        }
        {
            var Q0;
            Q0 = qSketchRegion(id + "F23", true);
            extrude(context, id + "F24", {"entities" : qUnion([Q0]), "operationType" : NewBodyOperationType.REMOVE, "endBound" : BoundingType.SYMMETRIC, "oppositeDirection" : true, "depth" : 1.27 * mm});
        }
        {
            var Q0;
            Q0 = qSketchRegion(id + "F23", true);
            extrude(context, id + "F25", {"entities" : qUnion([Q0]), "operationType" : NewBodyOperationType.REMOVE, "depth" : 7 * mm});
        }
        {
            var Q0;
            Q0 = qSketchRegion(id + "F21", true);
            extrude(context, id + "F26", {"entities" : qUnion([Q0]), "operationType" : NewBodyOperationType.ADD, "oppositeDirection" : true, "depth" : 6.35 * mm});
        }
        {
            var Q0;
            Q0=makeQuery(id+"F6.opExtrude","SWEPT_FACE",FACE,{"disambiguationData":[OSD([sQuery(id+"F5.wireOp",EDGE,"E33")])]});
            var sketch = newSketch(context, id + "F27", { "sketchPlane" : qUnion([Q0])});
            skCircle(sketch, "E122", {"center": v(-73.77, 6.35) * mm, "radius": 0.95 * mm});
            skSolve(sketch);
        }
        {
            var Q0;
            Q0 = qSketchRegion(id + "F27", true);
            extrude(context, id + "F28", {"entities" : qUnion([Q0]), "operationType" : NewBodyOperationType.ADD, "oppositeDirection" : true, "depth" : 7 * mm});
        }
        {
            var Q0;
            Q0 = qSketchRegion(id + "F27", true);
            extrude(context, id + "F29", {"entities" : qUnion([Q0]), "operationType" : NewBodyOperationType.ADD, "depth" : 1.27 * mm});
        }
        {
            var Q0;
            Q0=makeQuery(id+"F3.boolean.opBoolean","COPY",FACE,{"derivedFrom":makeQuery(id+"F3.opExtrude","SWEPT_FACE",FACE,{"disambiguationData":[OSD([sQuery(id+"F2.wireOp",EDGE,"E10.right")])]})});
            var sketch = newSketch(context, id + "F30", { "sketchPlane" : qUnion([Q0])});
            skCircle(sketch, "E123", {"center": v(73.77, 6.35) * mm, "radius": 0.95 * mm});
            skSolve(sketch);
        }
        {
            var Q0;
            Q0 = qSketchRegion(id + "F30", true);
            extrude(context, id + "F31", {"entities" : qUnion([Q0]), "operationType" : NewBodyOperationType.REMOVE, "depth" : 7 * mm});
        }
        {
            var Q0;
            Q0 = qSketchRegion(id + "F30", true);
            extrude(context, id + "F32", {"entities" : qUnion([Q0]), "operationType" : NewBodyOperationType.REMOVE, "oppositeDirection" : true, "depth" : 0.64 * mm});
        }
        {
            var Q0;
            Q0=makeQuery(id+"F6.opExtrude","SWEPT_FACE",FACE,{"disambiguationData":[OSD([sQuery(id+"F5.wireOp",EDGE,"E36")])]});
            var sketch = newSketch(context, id + "F33", { "sketchPlane" : qUnion([Q0])});
            skCircle(sketch, "E124", {"center": v(-74.59, 6.35) * mm, "radius": 0.95 * mm});
            skPoint(sketch, "E124.centerSnap0", {"position": v(-75.22, 6.35) * mm});
            skSolve(sketch);
        }
        {
            var Q0;
            Q0 = qSketchRegion(id + "F33", true);
            extrude(context, id + "F34", {"entities" : qUnion([Q0]), "operationType" : NewBodyOperationType.ADD, "oppositeDirection" : true, "depth" : 7 * mm});
        }
        {
            var Q0;
            Q0 = qSketchRegion(id + "F33", true);
            extrude(context, id + "F35", {"entities" : qUnion([Q0]), "operationType" : NewBodyOperationType.ADD, "depth" : 1.27 * mm});
        }
        {
            var Q0;
            Q0 = qSketchRegion(id + "F33", true);
            extrude(context, id + "F36", {"entities" : qUnion([Q0]), "operationType" : NewBodyOperationType.REMOVE, "depth" : 1.27 * mm});
        }
        {
            var Q0;
            Q0 = qSketchRegion(id + "F33", true);
            extrude(context, id + "F37", {"entities" : qUnion([Q0]), "operationType" : NewBodyOperationType.REMOVE, "oppositeDirection" : true, "depth" : 7 * mm});
        }
        {
            var Q0;
            Q0=makeQuery(id+"F6.opExtrude","SWEPT_FACE",FACE,{"disambiguationData":[OSD([sQuery(id+"F5.wireOp",EDGE,"E39")])]});
            var sketch = newSketch(context, id + "F38", { "sketchPlane" : qUnion([Q0])});
            skCircle(sketch, "E125", {"center": v(-71.3, 6.35) * mm, "radius": 0.95 * mm});
            skPoint(sketch, "E125.centerSnap0", {"position": v(-71.93, 6.35) * mm});
            skSolve(sketch);
        }
        {
            var Q0;
            Q0 = qSketchRegion(id + "F38", true);
            extrude(context, id + "F39", {"entities" : qUnion([Q0]), "operationType" : NewBodyOperationType.ADD, "oppositeDirection" : true, "depth" : 7 * mm});
        }
        {
            var Q0;
            Q0 = qSketchRegion(id + "F38", true);
            extrude(context, id + "F40", {"entities" : qUnion([Q0]), "operationType" : NewBodyOperationType.ADD, "depth" : 1.27 * mm});
        }
        {
            var Q0;
            Q0 = qSketchRegion(id + "F38", true);
            extrude(context, id + "F41", {"entities" : qUnion([Q0]), "operationType" : NewBodyOperationType.REMOVE, "depth" : 1.27 * mm});
        }
        {
            var Q0;
            Q0 = qSketchRegion(id + "F38", true);
            extrude(context, id + "F42", {"entities" : qUnion([Q0]), "operationType" : NewBodyOperationType.REMOVE, "oppositeDirection" : true, "depth" : 7 * mm});
        }
    });
